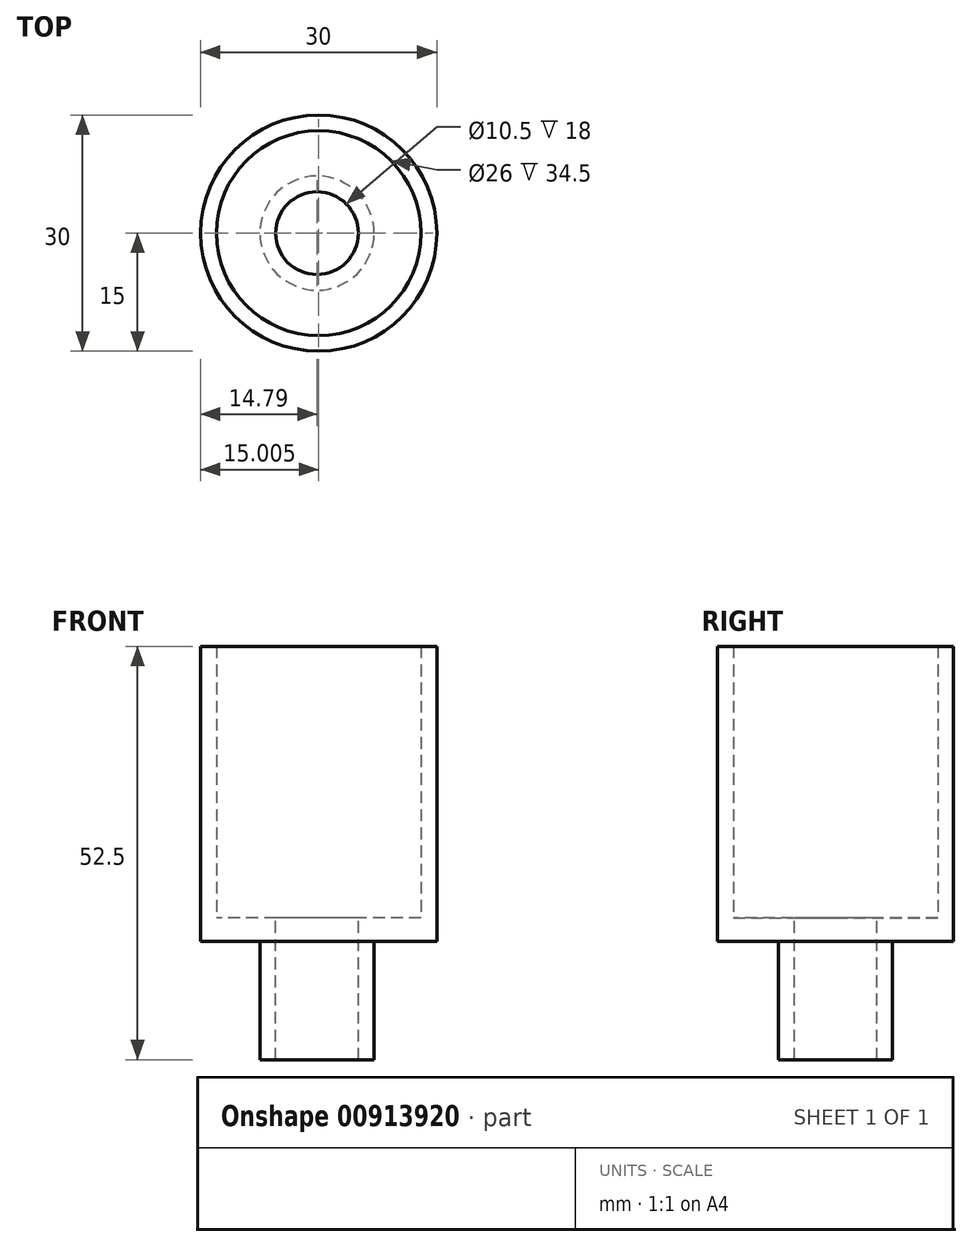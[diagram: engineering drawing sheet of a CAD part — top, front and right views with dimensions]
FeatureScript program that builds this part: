
annotation { "Feature Type Name" : "Feature", "Feature Type Description" : "" }
export const myFeature = defineFeature(function(context is Context, id is Id, definition is map)
    precondition{}
    {
        {
            var Q0;
            Q0=qCreatedBy(makeId("Top.planeOp"),FACE);
            var sketch = newSketch(context, id + "F0", { "sketchPlane" : qUnion([Q0])});
            skCircle(sketch, "E0", {"center": v(0, 0) * mm, "radius": 5.25 * mm});
            skCircle(sketch, "E1", {"center": v(0, 0) * mm, "radius": 7.25 * mm});
            skSolve(sketch);
        }
        {
            var Q0;
            Q0=qSketchRegion(id+"F0",true);
            extrude(context, id + "F1", {"entities" : qUnion([Q0]), "oppositeDirection" : true, "depth" : 15 * mm, "offsetDistance" : 25 * mm});
        }
        {
            var Q0;
            Q0=makeQuery(id+"F1.opExtrude","CAP_FACE",FACE,{"disambiguationData":[OSD([sQuery(id+"F0.wireOp",EDGE,"E0"),sQuery(id+"F0.wireOp",EDGE,"E1")])],"isStart":true});
            var sketch = newSketch(context, id + "F2", { "sketchPlane" : qUnion([Q0])});
            skCircle(sketch, "E2", {"center": v(0, 0) * mm, "radius": 5.25 * mm});
            skCircle(sketch, "E3", {"center": v(0.21, 0) * mm, "radius": 15 * mm});
            skSolve(sketch);
        }
        {
            var Q0;
            Q0=qSketchRegion(id+"F2",true);
            extrude(context, id + "F3", {"entities" : qUnion([Q0]), "operationType" : NewBodyOperationType.ADD, "depth" : 3 * mm, "offsetDistance" : 25 * mm});
        }
        {
            var Q0;
            Q0=makeQuery(id+"F3.opExtrude","CAP_FACE",FACE,{"disambiguationData":[OSD([sQuery(id+"F2.wireOp",EDGE,"E2"),sQuery(id+"F2.wireOp",EDGE,"E3")])],"isStart":false});
            var sketch = newSketch(context, id + "F4", { "sketchPlane" : qUnion([Q0])});
            skCircle(sketch, "E4", {"center": v(0.21, 0) * mm, "radius": 15 * mm});
            skPoint(sketch, "E4.first.point", {"position": v(-9.56, -11.37) * mm});
            skPoint(sketch, "E4.second.point", {"position": v(15.1, -1.92) * mm});
            skPoint(sketch, "E4.third.point", {"position": v(-1.49, 14.9) * mm});
            skCircle(sketch, "E5", {"center": v(0.21, 0) * mm, "radius": 13 * mm});
            skSolve(sketch);
        }
        {
            var Q0;
            Q0=qSketchRegion(id+"F4",true);
            extrude(context, id + "F5", {"entities" : qUnion([Q0]), "operationType" : NewBodyOperationType.ADD, "depth" : 34.5 * mm, "offsetDistance" : 25 * mm});
        }
    });
